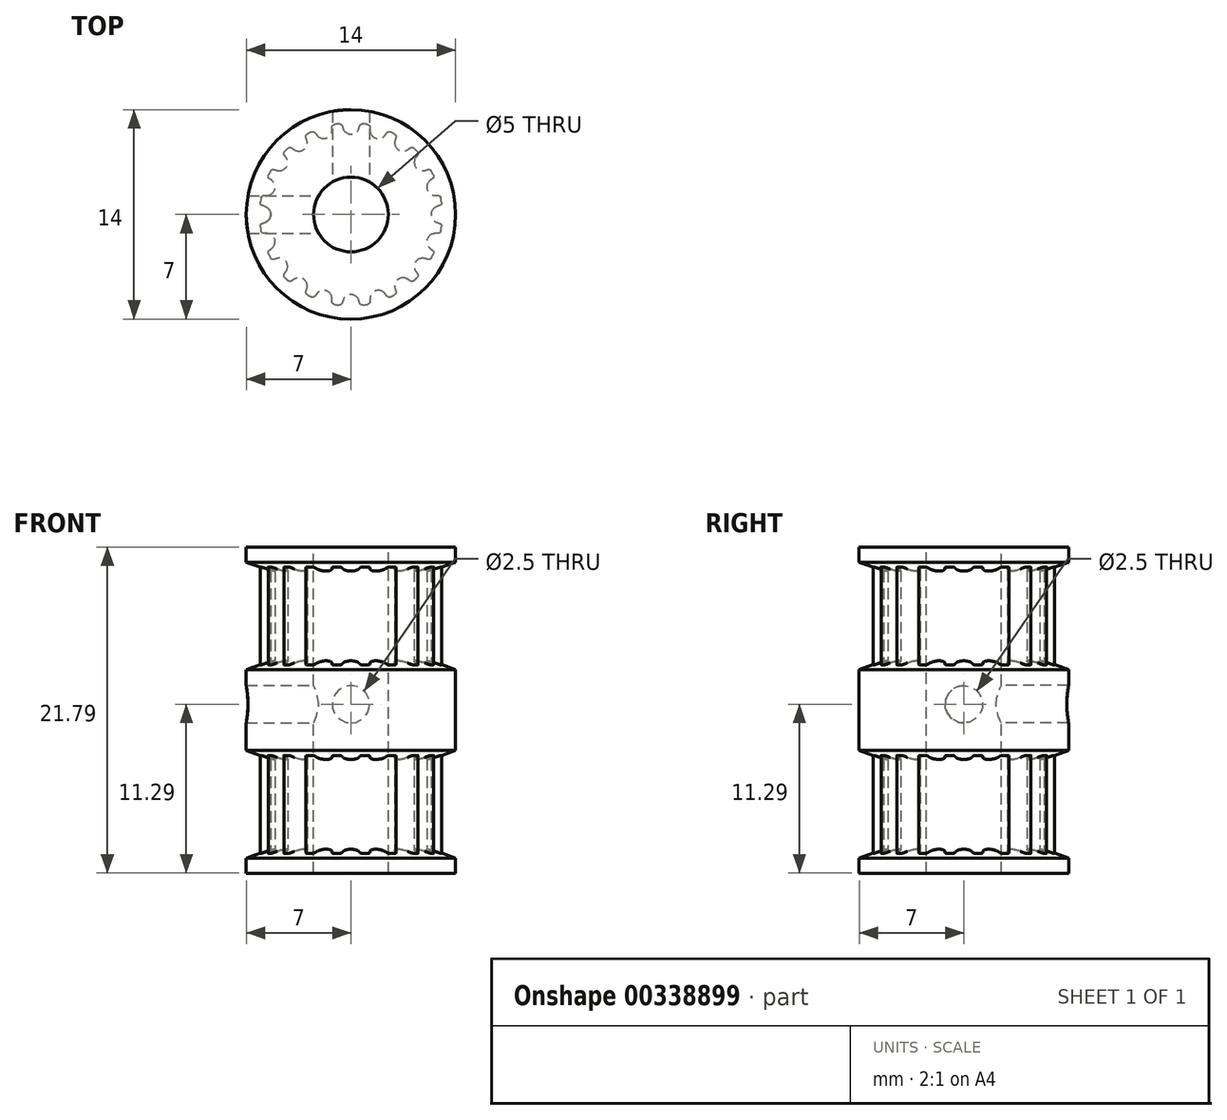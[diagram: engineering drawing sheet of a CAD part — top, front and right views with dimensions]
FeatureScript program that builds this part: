
annotation { "Feature Type Name" : "Feature", "Feature Type Description" : "" }
export const myFeature = defineFeature(function(context is Context, id is Id, definition is map)
    precondition{}
    {
        {
            assignVariable(context, id + "F0", {"name" : "teeth", "anyValue" : 20});
        }
        {
            assignVariable(context, id + "F1", {"name" : "total_length", "anyValue" : 21});
        }
        {
            var Q0;
            Q0=qCreatedBy(makeId("Top.planeOp"),FACE);
            var sketch = newSketch(context, id + "F2", { "sketchPlane" : qUnion([Q0])});
            skLineSegment(sketch, "E0", {"start": v(0, 0) * mm, "end": v(0, 5.36) * mm, "construction": true});
            skCircle(sketch, "E1", {"center": v(0, 0) * mm, "radius": 6.11 * mm});
            skPoint(sketch, "E2.MirrorCS.end.orphan", {"position": v(0.96, 6.04) * mm});
            skLineSegment(sketch, "E3", {"start": v(0.96, 6.04) * mm, "end": v(1, 6.29) * mm, "construction": true});
            skLineSegment(sketch, "E4", {"start": v(-0.96, 6.04) * mm, "end": v(-1, 6.29) * mm, "construction": true});
            skArc(sketch, "E5", {"start": v(0, 5.36) * mm, "mid": v(0.31, 5.46) * mm, "end": v(0.52, 5.72) * mm});
            skArc(sketch, "E6", {"start": v(0.52, 5.72) * mm, "mid": v(0.56, 5.83) * mm, "end": v(0.58, 5.94) * mm, "construction": true});
            skLineSegment(sketch, "E7", {"start": v(0, 5.36) * mm, "end": v(0, 6.11) * mm, "construction": true});
            skLineSegment(sketch, "E8", {"start": v(0, 6.11) * mm, "end": v(0, 6.37) * mm, "construction": true});
            skArc(sketch, "E9", {"start": v(0.58, 5.94) * mm, "mid": v(0.64, 6.04) * mm, "end": v(0.75, 6.07) * mm, "construction": true});
            skArc(sketch, "E10", {"start": v(1, 6.29) * mm, "mid": v(0, 6.37) * mm, "end": v(-1, 6.29) * mm, "construction": true});
            skLineSegment(sketch, "E11", {"start": v(0.96, 6.04) * mm, "end": v(0.84, 5.3) * mm});
            skLineSegment(sketch, "E12", {"start": v(0.84, 5.3) * mm, "end": v(0, 0) * mm});
            skLineSegment(sketch, "E13", {"start": v(0, 0) * mm, "end": v(-0.84, 5.3) * mm});
            skLineSegment(sketch, "E14", {"start": v(-0.84, 5.3) * mm, "end": v(-0.96, 6.04) * mm});
            skArc(sketch, "E15", {"start": v(0.8, 6.06) * mm, "mid": v(0.67, 6.03) * mm, "end": v(0.6, 5.93) * mm});
            skArc(sketch, "E16", {"start": v(0.52, 5.72) * mm, "mid": v(0.56, 5.83) * mm, "end": v(0.6, 5.93) * mm});
            skArc(sketch, "E17.MirrorCS", {"start": v(0, 5.36) * mm, "mid": v(-0.31, 5.46) * mm, "end": v(-0.52, 5.72) * mm});
            skArc(sketch, "E18.MirrorCS", {"start": v(-0.52, 5.72) * mm, "mid": v(-0.56, 5.83) * mm, "end": v(-0.6, 5.93) * mm});
            skArc(sketch, "E19.MirrorCS", {"start": v(-0.8, 6.06) * mm, "mid": v(-0.67, 6.03) * mm, "end": v(-0.6, 5.93) * mm});
            skArc(sketch, "E20", {"start": v(0, 6.11) * mm, "mid": v(-0.2, 6.1) * mm, "end": v(-0.4, 6.1) * mm});
            skArc(sketch, "E21", {"start": v(0.84, 5.3) * mm, "mid": v(0, 5.36) * mm, "end": v(-0.84, 5.3) * mm, "construction": true});
            skLineSegment(sketch, "E22", {"start": v(1, 6.29) * mm, "end": v(1.05, 6.66) * mm, "construction": true});
            skLineSegment(sketch, "E23", {"start": v(-1, 6.29) * mm, "end": v(-1.05, 6.66) * mm, "construction": true});
            skArc(sketch, "E24", {"start": v(-1.05, 6.66) * mm, "mid": v(0, 6.74) * mm, "end": v(1.05, 6.66) * mm, "construction": true});
            skSolve(sketch);
        }
        {
            var Q0;
            Q0=makeQuery(id+"F2.imprint","IMPRINT",FACE,{"disambiguationData":[TD([[makeQuery(id+"F2.imprint","IMPRINT",EDGE,{"derivedFrom":sQuery(id+"F2.wireOp",EDGE,"E5")}),-1.0]])]});
            var Q1;
            {var subQ1=sQuery(id+"F2.wireOp",EDGE,"E14");Q1=makeQuery(id+"F2.imprint","IMPRINT",FACE,{"disambiguationData":[TD([[makeQuery(id+"F2.imprint","IMPRINT",EDGE,{"derivedFrom":subQ1}),-1.0]])]});}
            var Q2;
            {var subQ0=sQuery(id+"F2.wireOp",EDGE,"E12");Q2=makeQuery(id+"F2.imprint","IMPRINT",FACE,{"disambiguationData":[TD([[makeQuery(id+"F2.imprint","IMPRINT",EDGE,{"derivedFrom":subQ0}),-1.0]])]});}
            extrude(context, id + "F3", {"entities" : qUnion([Q0, Q1, Q2]), "endBound" : BoundingType.SYMMETRIC, "depth" : (getVariable(context, 'total_length')) * mm});
        }
        {
            var Q0;
            Q0=makeQuery(id+"F3.opExtrude","SWEPT_BODY",BODY,{"disambiguationData":[OSD([sQuery(id+"F2.wireOp",EDGE,"E1"),sQuery(id+"F2.wireOp",EDGE,"E5"),sQuery(id+"F2.wireOp",EDGE,"E11"),sQuery(id+"F2.wireOp",EDGE,"E12"),sQuery(id+"F2.wireOp",EDGE,"E13"),sQuery(id+"F2.wireOp",EDGE,"E14"),sQuery(id+"F2.wireOp",EDGE,"E15"),sQuery(id+"F2.wireOp",EDGE,"E16"),sQuery(id+"F2.wireOp",EDGE,"E17.MirrorCS"),sQuery(id+"F2.wireOp",EDGE,"E18.MirrorCS"),sQuery(id+"F2.wireOp",EDGE,"E19.MirrorCS")])]});
            var Q1;
            Q1=makeQuery(id+"F3.opExtrude","SWEPT_EDGE",EDGE,{"disambiguationData":[OSD([sQuery(id+"F2.wireOp",EDGE,"E12"),sQuery(id+"F2.wireOp",EDGE,"E13")])]});
            circularPattern(context, id + "F4", {"operationType" : NewBodyOperationType.ADD, "entities" : qUnion([Q0]), "axis" : qUnion([Q1]), "angle" : 360 * degree, "instanceCount" : getVariable(context, 'teeth'), "equalSpace" : true});
        }
        {
            var Q0;
            Q0=qCreatedBy(makeId("Front.planeOp"),FACE);
            var sketch = newSketch(context, id + "F5", { "sketchPlane" : qUnion([Q0])});
            skLineSegment(sketch, "E25", {"start": v(0, 10.5) * mm, "end": v(7, 10.5) * mm});
            skLineSegment(sketch, "E26", {"start": v(7, 10.5) * mm, "end": v(7, 9.5) * mm});
            skLineSegment(sketch, "E27", {"start": v(7, 9.5) * mm, "end": v(5.36, 8.9) * mm});
            skLineSegment(sketch, "E28", {"start": v(5.36, 8.9) * mm, "end": v(0, 8.9) * mm});
            skLineSegment(sketch, "E29", {"start": v(0, 8.9) * mm, "end": v(0, 10.5) * mm});
            skLineSegment(sketch, "E30", {"start": v(0, 2.9) * mm, "end": v(5.36, 2.9) * mm});
            skLineSegment(sketch, "E31", {"start": v(5.36, 2.9) * mm, "end": v(7, 2.3) * mm});
            skLineSegment(sketch, "E32", {"start": v(7, 2.3) * mm, "end": v(7, -3.1) * mm});
            skLineSegment(sketch, "E33", {"start": v(7, -3.1) * mm, "end": v(5.36, -3.7) * mm});
            skLineSegment(sketch, "E34", {"start": v(5.36, -3.7) * mm, "end": v(0, -3.7) * mm});
            skLineSegment(sketch, "E35", {"start": v(0, -3.7) * mm, "end": v(0, 2.9) * mm});
            skLineSegment(sketch, "E36", {"start": v(0, -9.7) * mm, "end": v(5.36, -9.7) * mm});
            skLineSegment(sketch, "E37", {"start": v(5.36, -9.7) * mm, "end": v(7, -10.3) * mm});
            skLineSegment(sketch, "E38", {"start": v(7, -10.3) * mm, "end": v(7, -11.3) * mm});
            skLineSegment(sketch, "E39", {"start": v(7, -11.3) * mm, "end": v(0, -11.3) * mm});
            skLineSegment(sketch, "E40", {"start": v(0, -11.3) * mm, "end": v(0, -9.7) * mm});
            skSolve(sketch);
        }
        {
            var Q0;
            Q0=qSketchRegion(id+"F5",true);
            var Q1;
            Q1=sQuery(id+"F5.wireOp",EDGE,"E35");
            revolve(context, id + "F6", {"operationType" : NewBodyOperationType.ADD, "entities" : qUnion([Q0]), "axis" : qUnion([Q1]), "revolveType" : RevolveType.FULL});
        }
        {
            var Q0;
            Q0=qCreatedBy(makeId("Top.planeOp"),FACE);
            var sketch = newSketch(context, id + "F7", { "sketchPlane" : qUnion([Q0])});
            skCircle(sketch, "E41", {"center": v(0, 0) * mm, "radius": 2.5 * mm});
            skSolve(sketch);
        }
        {
            var Q0;
            Q0=qSketchRegion(id+"F7",true);
            extrude(context, id + "F8", {"entities" : qUnion([Q0]), "operationType" : NewBodyOperationType.REMOVE, "endBound" : BoundingType.SYMMETRIC, "oppositeDirection" : true, "depth" : 100 * mm});
        }
        {
            var Q0;
            Q0=qCreatedBy(makeId("Front.planeOp"),FACE);
            var sketch = newSketch(context, id + "F9", { "sketchPlane" : qUnion([Q0])});
            skCircle(sketch, "E42", {"center": v(0, 0) * mm, "radius": 1.25 * mm});
            skSolve(sketch);
        }
        {
            var Q0;
            Q0 = qSketchRegion(id + "F9", true);
            extrude(context, id + "F10", {"entities" : qUnion([Q0]), "operationType" : NewBodyOperationType.REMOVE, "oppositeDirection" : true, "depth" : 25 * mm});
        }
        {
            var Q0;
            Q0=qCreatedBy(makeId("Right.planeOp"),FACE);
            var sketch = newSketch(context, id + "F11", { "sketchPlane" : qUnion([Q0])});
            skCircle(sketch, "E43", {"center": v(0, 0) * mm, "radius": 1.25 * mm});
            skSolve(sketch);
        }
        {
            var Q0;
            Q0 = qSketchRegion(id + "F11", true);
            extrude(context, id + "F12", {"entities" : qUnion([Q0]), "operationType" : NewBodyOperationType.REMOVE, "oppositeDirection" : true, "depth" : 25 * mm});
        }
    });
